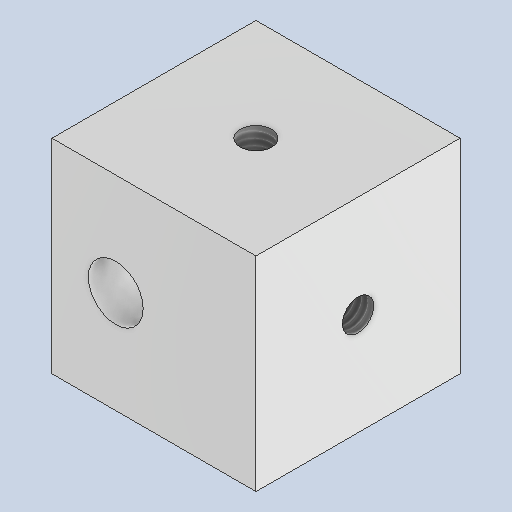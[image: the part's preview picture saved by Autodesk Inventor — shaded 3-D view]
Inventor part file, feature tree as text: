
AUTODESK INVENTOR PART (.ipt)
format: ipt  version: 2025 (Build 290162010, 162A)  size: 162,816 bytes
history: native  units: mm
features: sketch x4, hole x3, extrude x1
ambient origin geometry x8: Origin, YZ Plane, XZ Plane, XY Plane, X Axis, Y Axis, Z Axis, Center Point
bodies: Volumenkörper1 (feature_tree)
feature tree (8):
  extrude  "Extrusion1"  Depth=16.0mm
  hole  "Bohrung1"  [1 undecoded]
  hole  "Bohrung2"  [1 undecoded]
  hole  "Bohrung3"  [1 undecoded]
  sketch  "Skizze1"  dims[d0=16.0mm d1=16.0mm]
  sketch  "Skizze2"  dims[d2=16.0mm d3=0.0mm d4=5.0mm]
  sketch  "Skizze3"  dims[d5=4.3mm d6=6.0mm d7=11.0mm d8=2.0mm d9=90.0deg d10=8.0mm d11=20.594885mm d12=8.0mm]
  sketch  "Skizze4"  dims[d13=2.459mm d14=6.0mm d15=11.0mm d16=2.0mm d17=90.0deg d18=8.0mm d19=20.594885mm d20=8.0mm d21=2.459mm d22=6.0mm d23=4.0mm d24=2.0mm d25=90.0deg d26=8.0mm d27=20.594885mm]
note: 3 required parameter values undecoded (feature->parameter linkage not recoverable at this tier; creation-order binding heuristic only, values carry confidence <= 0.55)
